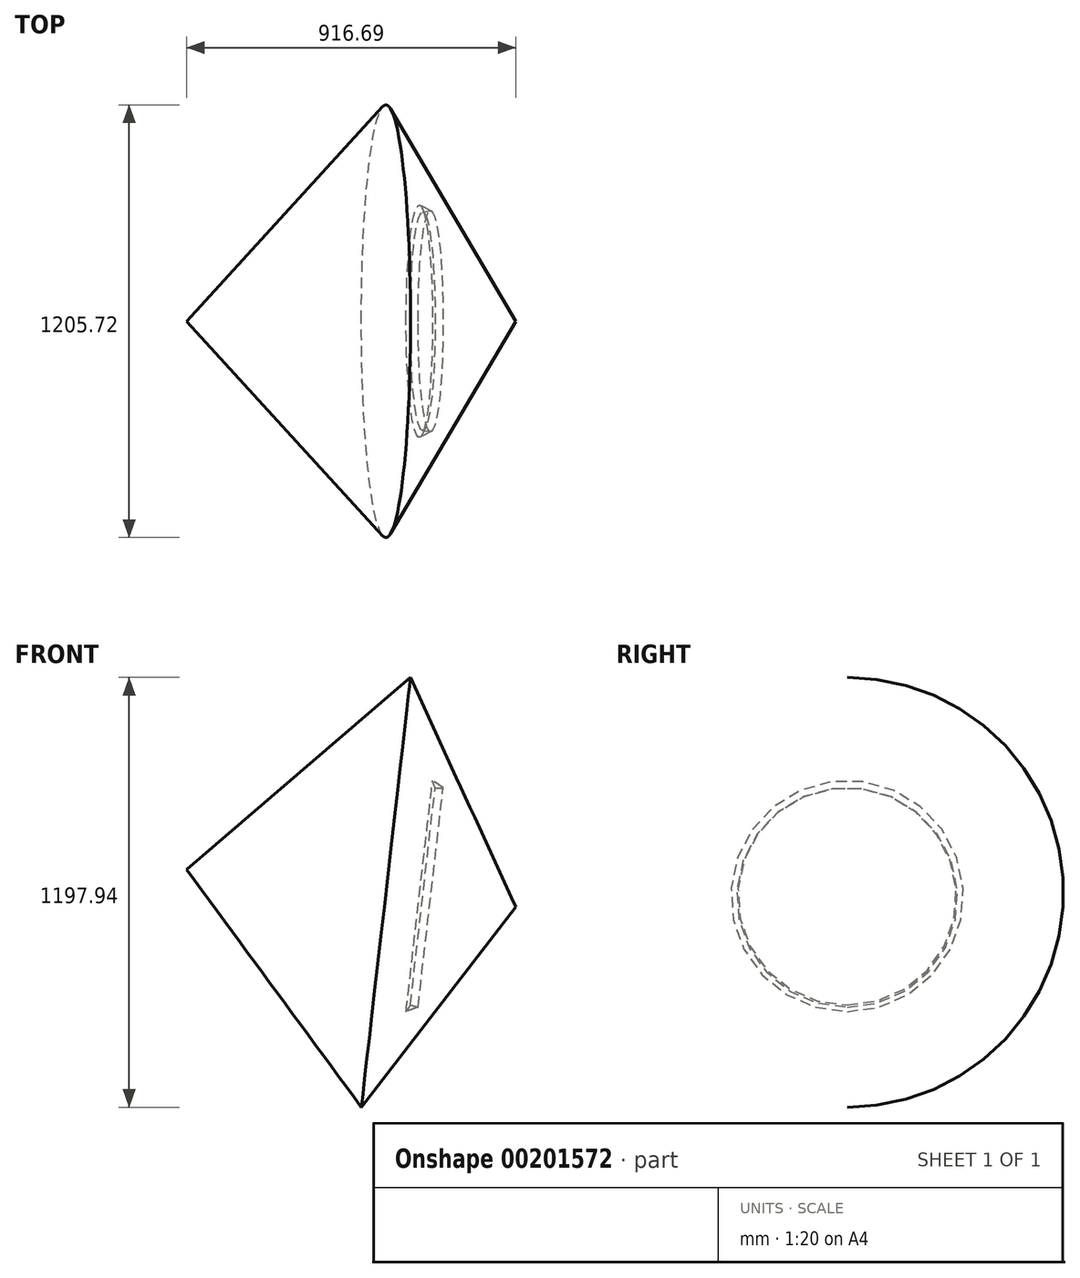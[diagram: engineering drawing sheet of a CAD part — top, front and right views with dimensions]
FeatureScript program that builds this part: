
annotation { "Feature Type Name" : "Feature", "Feature Type Description" : "" }
export const myFeature = defineFeature(function(context is Context, id is Id, definition is map)
    precondition{}
    {
        {
            var Q0;
            Q0=qCreatedBy(makeId("Front.planeOp"),FACE);
            var sketch = newSketch(context, id + "F0", { "sketchPlane" : qUnion([Q0])});
            skLineSegment(sketch, "E0", {"start": v(-37.33, 57.81) * mm, "end": v(-37.33, 47.93) * mm});
            skLineSegment(sketch, "E1", {"start": v(-37.33, 47.93) * mm, "end": v(-37.33, 36.42) * mm});
            skLineSegment(sketch, "E2", {"start": v(-37.33, 36.42) * mm, "end": v(-45.6, 33) * mm});
            skLineSegment(sketch, "E3", {"start": v(-45.6, 33) * mm, "end": v(-45.6, 23.5) * mm});
            skLineSegment(sketch, "E4", {"start": v(-45.6, 23.5) * mm, "end": v(-37.33, 23.5) * mm});
            skLineSegment(sketch, "E5", {"start": v(-37.33, 23.5) * mm, "end": v(-45.6, 17.66) * mm});
            skLineSegment(sketch, "E6", {"start": v(-45.6, 17.66) * mm, "end": v(-37.33, 11.4) * mm});
            skLineSegment(sketch, "E7", {"start": v(-37.33, 11.4) * mm, "end": v(-23.6, 11.4) * mm});
            skLineSegment(sketch, "E8", {"start": v(-23.6, 11.4) * mm, "end": v(-23.6, 57.81) * mm});
            skLineSegment(sketch, "E9", {"start": v(-23.6, 57.81) * mm, "end": v(-37.33, 57.81) * mm});
            skSolve(sketch);
        }
        {
            var Q0;
            Q0=makeQuery(id+"F0.imprint","IMPRINT",FACE,{"disambiguationData":[TD([[makeQuery(id+"F0.imprint","IMPRINT",EDGE,{"derivedFrom":sQuery(id+"F0.wireOp",EDGE,"E0")}),1.0]])]});
            var Q1;
            Q1=sQuery(id+"F0.wireOp",EDGE,"E8");
            revolve(context, id + "F1", {"entities" : qUnion([Q0]), "axis" : qUnion([Q1]), "revolveType" : RevolveType.FULL});
        }
        {
            var Q0;
            Q0=qCreatedBy(makeId("Front.planeOp"),FACE);
            var sketch = newSketch(context, id + "F2", { "sketchPlane" : qUnion([Q0])});
            skLineSegment(sketch, "E10", {"start": v(27.24, 37.84) * mm, "end": v(15.54, 19.67) * mm});
            skLineSegment(sketch, "E11", {"start": v(15.54, 19.67) * mm, "end": v(48.83, 32.19) * mm});
            skLineSegment(sketch, "E12", {"start": v(48.83, 32.19) * mm, "end": v(27.24, 37.84) * mm});
            skLineSegment(sketch, "E13", {"start": v(27.24, 32.19) * mm, "end": v(34.05, -24.32) * mm});
            skLineSegment(sketch, "E14", {"start": v(34.05, -24.32) * mm, "end": v(-595.63, 415.31) * mm});
            skLineSegment(sketch, "E15", {"start": v(-595.63, 415.31) * mm, "end": v(-108.97, -247) * mm});
            skLineSegment(sketch, "E16", {"start": v(-108.97, -247) * mm, "end": v(321.06, 310.68) * mm});
            skLineSegment(sketch, "E17", {"start": v(321.06, 310.68) * mm, "end": v(-595.63, 415.31) * mm});
            skSolve(sketch);
        }
        {
            var Q0;
            {var subQ3=sQuery(id+"F2.wireOp",EDGE,"E10");Q0=makeQuery(id+"F2.imprint","IMPRINT",FACE,{"disambiguationData":[TD([[makeQuery(id+"F2.imprint","IMPRINT",EDGE,{"derivedFrom":subQ3}),-1.0]])]});}
            var Q1;
            Q1=sQuery(id+"F2.wireOp",EDGE,"E17");
            revolve(context, id + "F3", {"operationType" : NewBodyOperationType.ADD, "entities" : qUnion([Q0]), "axis" : qUnion([Q1]), "revolveType" : RevolveType.FULL});
        }
    });
